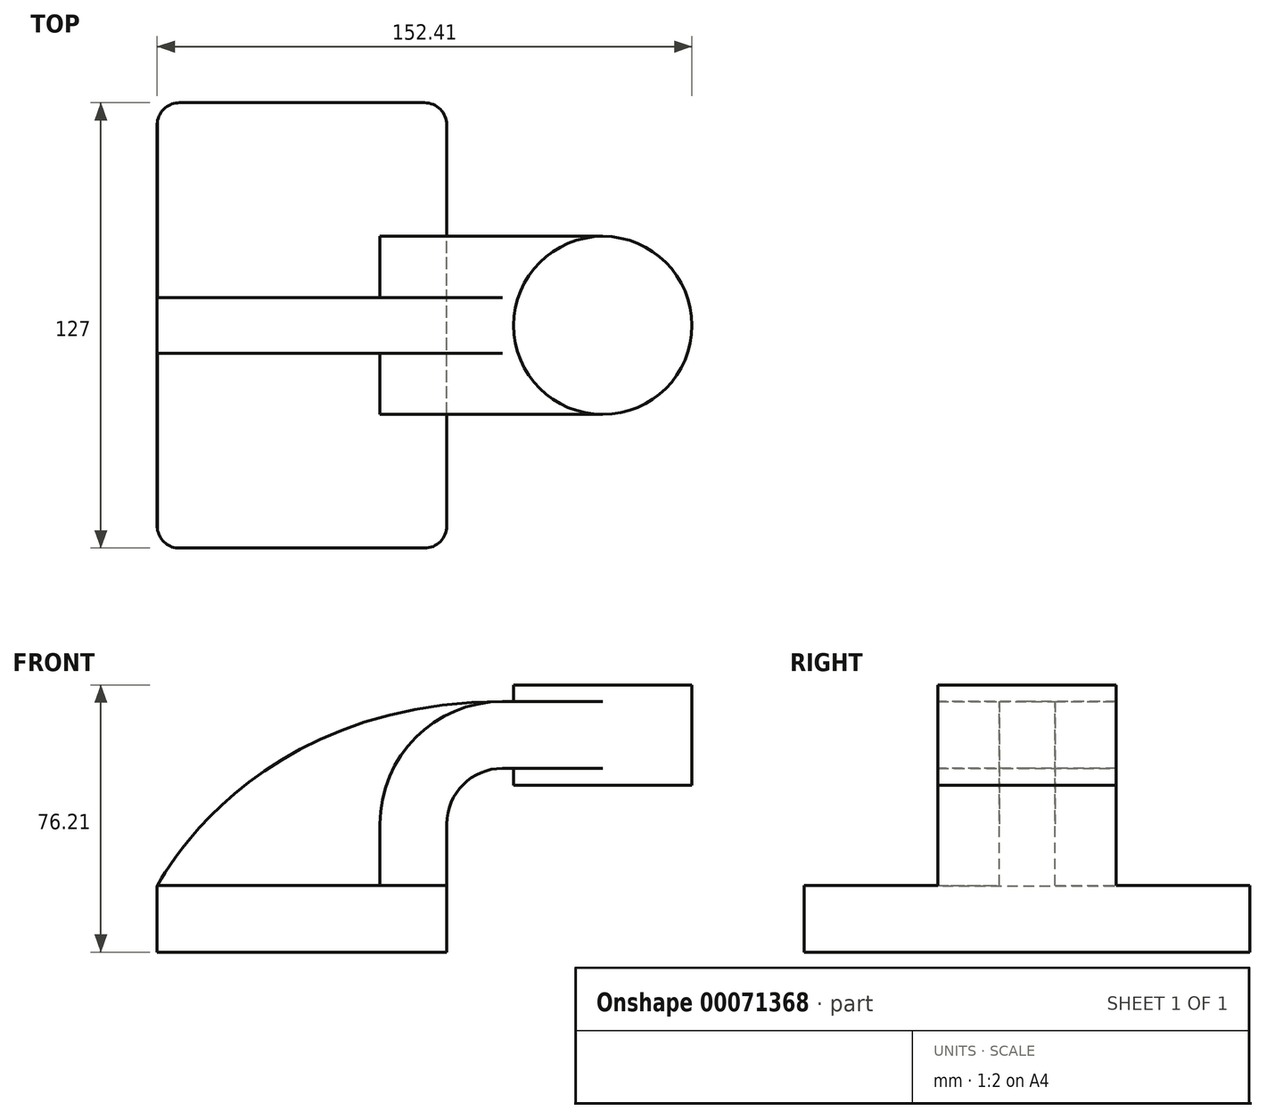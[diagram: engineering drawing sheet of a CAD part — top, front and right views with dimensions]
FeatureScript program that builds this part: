
annotation { "Feature Type Name" : "Feature", "Feature Type Description" : "" }
export const myFeature = defineFeature(function(context is Context, id is Id, definition is map)
    precondition{}
    {
        {
            var Q0;
            Q0=qCreatedBy(makeId("Front.planeOp"),FACE);
            var sketch = newSketch(context, id + "F0", { "sketchPlane" : qUnion([Q0])});
            skLineSegment(sketch, "E0.rect.bottom", {"start": v(-41.28, -9.53) * mm, "end": v(41.28, -9.53) * mm});
            skLineSegment(sketch, "E0.rect.top", {"start": v(-41.28, 9.53) * mm, "end": v(41.28, 9.53) * mm});
            skLineSegment(sketch, "E0.rect.left", {"start": v(-41.28, -9.53) * mm, "end": v(-41.28, 9.53) * mm});
            skLineSegment(sketch, "E0.rect.right", {"start": v(41.28, -9.53) * mm, "end": v(41.28, 9.53) * mm});
            skPoint(sketch, "E0.rect.middle", {"position": v(0, 0) * mm});
            skLineSegment(sketch, "E1.rect.bottom", {"start": v(111.12, 38.1) * mm, "end": v(60.32, 38.1) * mm});
            skLineSegment(sketch, "E1.rect.top", {"start": v(111.12, 66.68) * mm, "end": v(60.32, 66.68) * mm});
            skLineSegment(sketch, "E1.rect.left", {"start": v(111.12, 38.1) * mm, "end": v(111.12, 66.68) * mm});
            skLineSegment(sketch, "E1.rect.right", {"start": v(60.32, 38.1) * mm, "end": v(60.32, 66.67) * mm});
            skPoint(sketch, "E1.rect.middle", {"position": v(85.72, 52.39) * mm});
            skArc(sketch, "E2", {"start": v(57.15, 42.88) * mm, "mid": v(45.92, 38.23) * mm, "end": v(41.28, 27) * mm});
            skLineSegment(sketch, "E3", {"start": v(57.15, 42.88) * mm, "end": v(85.97, 42.88) * mm});
            skLineSegment(sketch, "E4", {"start": v(41.28, 9.53) * mm, "end": v(41.28, 27) * mm});
            skLineSegment(sketch, "E5.0", {"start": v(57.15, 61.93) * mm, "end": v(85.72, 61.93) * mm});
            skArc(sketch, "E5.1", {"start": v(57.15, 61.93) * mm, "mid": v(32.45, 51.7) * mm, "end": v(22.23, 27) * mm});
            skLineSegment(sketch, "E5.2", {"start": v(22.23, 9.53) * mm, "end": v(22.23, 27) * mm});
            skLineSegment(sketch, "E6", {"start": v(85.72, 38.1) * mm, "end": v(85.72, 66.68) * mm});
            skFitSpline(sketch, "E7", {"points": [v(-41.55, 9.26) * mm, v(-41.27, 9.26) * mm, v(57.15, 61.93) * mm], "startDerivative": vector(17.61, 0) * mm, "endDerivative": vector(225.95, 0) * mm});
            skPoint(sketch, "E8", {"position": v(85.72, 66.68) * mm});
            skSolve(sketch);
        }
        {
            var Q0;
            {var subQ1=sQuery(id+"F0.wireOp",EDGE,"E0.rect.bottom");Q0=makeQuery(id+"F0.imprint","IMPRINT",FACE,{"disambiguationData":[TD([[makeQuery(id+"F0.imprint","IMPRINT",EDGE,{"derivedFrom":subQ1}),1.0]])]});}
            extrude(context, id + "F1", {"entities" : qUnion([Q0]), "depth" : 127 * mm, "symmetric" : true});
        }
        {
            var Q0;
            {var subQ0=sQuery(id+"F0.wireOp",EDGE,"E2");Q0=makeQuery(id+"F0.imprint","IMPRINT",FACE,{"disambiguationData":[TD([[makeQuery(id+"F0.imprint","IMPRINT",EDGE,{"derivedFrom":subQ0}),-1.0]])]});}
            extrude(context, id + "F2", {"entities" : qUnion([Q0]), "operationType" : NewBodyOperationType.ADD, "depth" : 50.8 * mm, "symmetric" : true});
        }
        {
            var Q0;
            {var subQ4=sQuery(id+"F0.wireOp",EDGE,"E5.1");Q0=makeQuery(id+"F0.imprint","IMPRINT",FACE,{"disambiguationData":[TD([[makeQuery(id+"F0.imprint","IMPRINT",EDGE,{"derivedFrom":subQ4}),-1.0]])]});}
            extrude(context, id + "F3", {"entities" : qUnion([Q0]), "operationType" : NewBodyOperationType.ADD, "depth" : 15.88 * mm, "symmetric" : true});
        }
        {
            var Q0;
            {var subQ0=sQuery(id+"F0.wireOp",EDGE,"E3");var subQ1=sQuery(id+"F0.wireOp",EDGE,"E1.rect.right");var subQ2=makeQuery(id+"F0.imprint","INTERSECT",VERTEX,{"derivedFrom":[subQ1,subQ0]});Q0=makeQuery(id+"F0.imprint","IMPRINT",FACE,{"disambiguationData":[TD([[makeQuery(id+"F0.imprint","IMPRINT",EDGE,{"disambiguationData":[TD([[subQ2,-1.0]])],"derivedFrom":subQ1}),-1.0]])]});}
            extrude(context, id + "F4", {"entities" : qUnion([Q0]), "operationType" : NewBodyOperationType.ADD, "depth" : 50.8 * mm, "symmetric" : true});
        }
        {
            var Q0;
            {var subQ4=sQuery(id+"F0.wireOp",EDGE,"E1.rect.left");Q0=makeQuery(id+"F0.imprint","IMPRINT",FACE,{"disambiguationData":[TD([[makeQuery(id+"F0.imprint","IMPRINT",EDGE,{"derivedFrom":subQ4}),1.0]])]});}
            var Q1;
            Q1=sQuery(id+"F0.wireOp",EDGE,"E6");
            revolve(context, id + "F5", {"operationType" : NewBodyOperationType.ADD, "entities" : qUnion([Q0]), "axis" : qUnion([Q1]), "revolveType" : RevolveType.FULL});
        }
        {
            var Q0;
            Q0=makeQuery(id+"F1.opExtrude","CAP_EDGE",EDGE,{"disambiguationData":[OSD([sQuery(id+"F0.wireOp",EDGE,"E0.rect.right")])],"isStart":false});
            var Q1;
            Q1=makeQuery(id+"F1.opExtrude","CAP_EDGE",EDGE,{"disambiguationData":[OSD([sQuery(id+"F0.wireOp",EDGE,"E0.rect.left")])],"isStart":false});
            var Q2;
            Q2=makeQuery(id+"F1.opExtrude","CAP_EDGE",EDGE,{"disambiguationData":[OSD([sQuery(id+"F0.wireOp",EDGE,"E0.rect.left")])],"isStart":true});
            var Q3;
            Q3=makeQuery(id+"F1.opExtrude","CAP_EDGE",EDGE,{"disambiguationData":[OSD([sQuery(id+"F0.wireOp",EDGE,"E0.rect.right")])],"isStart":true});
            fillet(context, id + "F6", {"entities" : qUnion([Q0, Q1, Q2, Q3]), "radius" : 6.35 * mm, "tangentPropagation" : true, "allowEdgeOverflow" : false});
        }
    });
